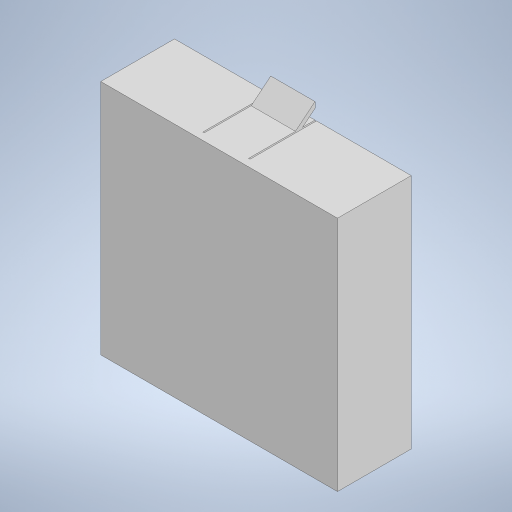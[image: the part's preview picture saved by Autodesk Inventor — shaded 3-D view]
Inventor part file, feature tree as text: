
AUTODESK INVENTOR PART (.ipt)
format: ipt  version: 2023 (Build 270158000, 158)  size: 257,536 bytes
history: native  units: in
note: dims shown in document units (in); Inventor stores cm internally (conversion verified against a paired STEP export)
features: projected_geometry x6, extrude x5, sketch x5, plane x1
ambient origin geometry x8: Origin, YZ Plane, XZ Plane, XY Plane, X Axis, Y Axis, Z Axis, Center Point
bodies: Solid1 (feature_tree)
feature tree (17):
  extrude  "Extrusion1"  Depth=3.01in
  extrude  "Extrusion2"  Depth=1.505in
  extrude  "Extrusion3"  Depth=0.1in
  plane  "Work Plane1"
  extrude  "Extrusion4"  Depth=0.6in
  extrude  "Extrusion5"  Depth=0.02in
  sketch  "Sketch1"  dims[d0=3.01in d1=3.01in]
  sketch  "Sketch2"  dims[d2=1.505in d3=1.505in]
  projected_geometry  "Projected Loop1"
  sketch  "Sketch3"  dims[d4=0.1in d5=0.0in d6=0.1in]
  projected_geometry  "Projected Loop2"
  sketch  "Sketch6"  dims[d7=1.0in d8=0.0in d9=0.6in]
  projected_geometry  "Projected Loop3"
  projected_geometry  "Projected Loop4"
  projected_geometry  "Projected Loop5"
  sketch  "Sketch7"  dims[d10=0.3in d11=0.02in d12=0.02in d13=1.0in d14=0.0in d19=-0.1in d20=0.126in d21=0.124in d22=0.05in d23=0.4in d24=0.0in d25=0.6in d26=0.0in]
  projected_geometry  "Projected Loop6"
